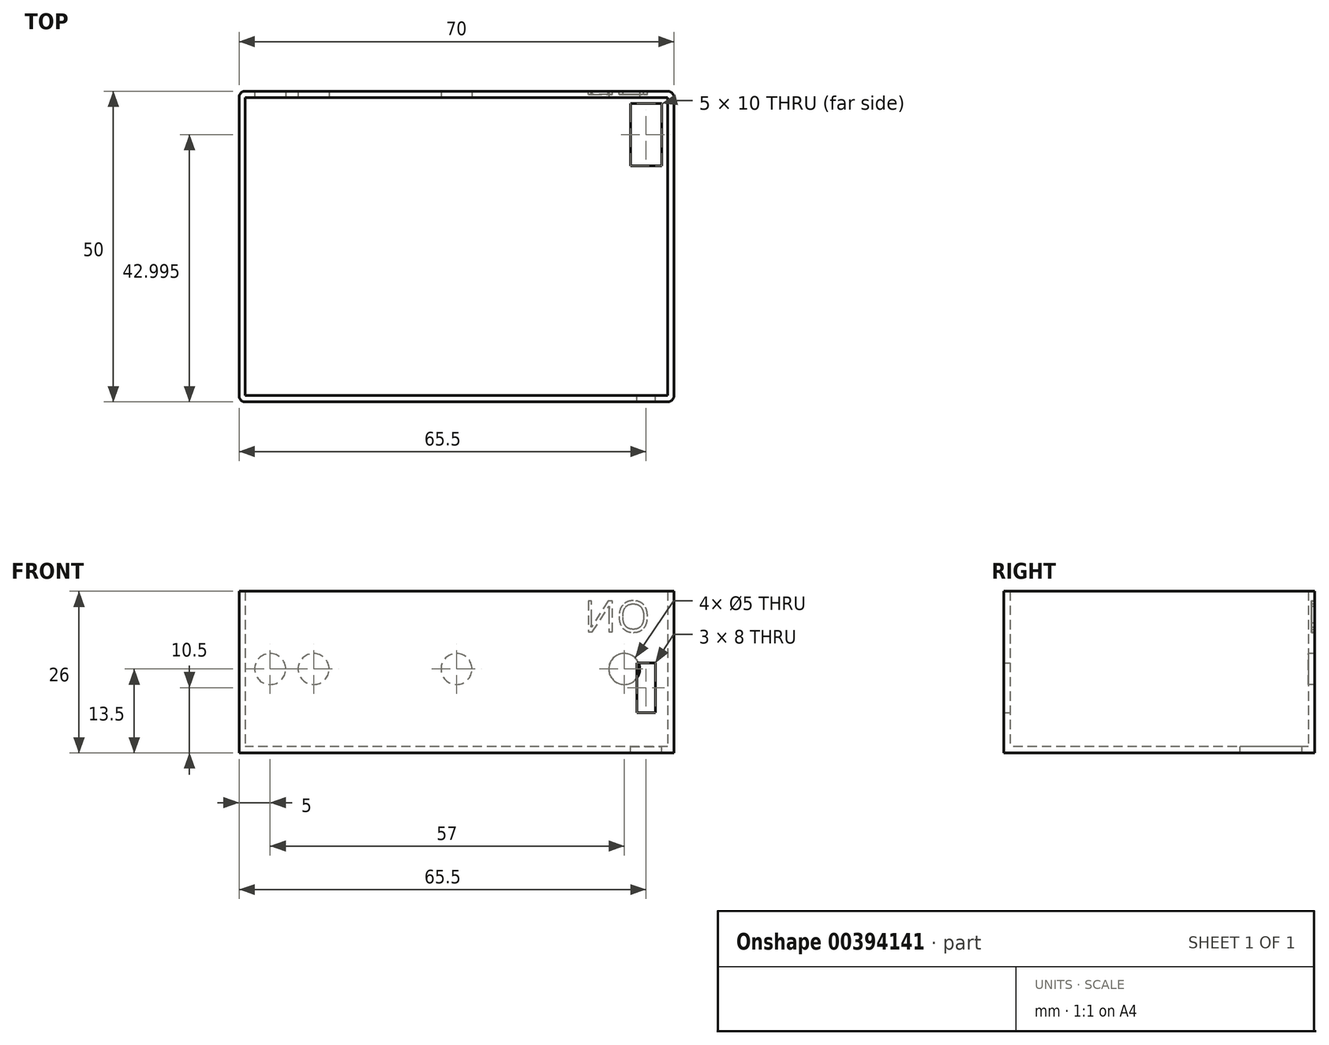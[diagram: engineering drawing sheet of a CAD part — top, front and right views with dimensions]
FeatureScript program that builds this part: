
annotation { "Feature Type Name" : "Feature", "Feature Type Description" : "" }
export const myFeature = defineFeature(function(context is Context, id is Id, definition is map)
    precondition{}
    {
        {
            var Q0;
            Q0=qCreatedBy(makeId("Top.planeOp"),FACE);
            var sketch = newSketch(context, id + "F0", { "sketchPlane" : qUnion([Q0])});
            skLineSegment(sketch, "E0.bottom", {"start": v(35, -25.8) * mm, "end": v(-35, -25.8) * mm});
            skLineSegment(sketch, "E0.top", {"start": v(35, 24.2) * mm, "end": v(-35, 24.2) * mm});
            skLineSegment(sketch, "E0.left", {"start": v(35, -25.8) * mm, "end": v(35, 24.2) * mm});
            skLineSegment(sketch, "E0.right", {"start": v(-35, -25.8) * mm, "end": v(-35, 24.2) * mm});
            skPoint(sketch, "E0.middle", {"position": v(0, -0.8) * mm});
            skSolve(sketch);
        }
        {
            var Q0;
            Q0 = qSketchRegion(id + "F0", true);
            extrude(context, id + "F1", {"entities" : qUnion([Q0]), "depth" : 1 * mm});
        }
        {
            var Q0;
            Q0=makeQuery(id+"F1.opExtrude","CAP_FACE",FACE,{"disambiguationData":[OSD([sQuery(id+"F0.wireOp",EDGE,"E0.bottom"),sQuery(id+"F0.wireOp",EDGE,"E0.top"),sQuery(id+"F0.wireOp",EDGE,"E0.left"),sQuery(id+"F0.wireOp",EDGE,"E0.right")])],"isStart":false});
            var sketch = newSketch(context, id + "F2", { "sketchPlane" : qUnion([Q0])});
            skLineSegment(sketch, "E1.0.0", {"start": v(35, -25.8) * mm, "end": v(35, 24.2) * mm});
            skLineSegment(sketch, "E1.0.1", {"start": v(35, 24.2) * mm, "end": v(-35, 24.2) * mm});
            skLineSegment(sketch, "E1.0.2", {"start": v(-35, 24.2) * mm, "end": v(-35, -25.8) * mm});
            skLineSegment(sketch, "E1.0.3", {"start": v(-35, -25.8) * mm, "end": v(35, -25.8) * mm});
            skLineSegment(sketch, "E2.0", {"start": v(-34, 23.2) * mm, "end": v(-34, -24.8) * mm});
            skLineSegment(sketch, "E2.1", {"start": v(34, 23.2) * mm, "end": v(-34, 23.2) * mm});
            skLineSegment(sketch, "E2.2", {"start": v(34, -24.8) * mm, "end": v(34, 23.2) * mm});
            skLineSegment(sketch, "E2.3", {"start": v(-34, -24.8) * mm, "end": v(34, -24.8) * mm});
            skSolve(sketch);
        }
        {
            var Q0;
            Q0=makeQuery(id+"F2.imprint","IMPRINT",FACE,{"disambiguationData":[TD([[makeQuery(id+"F2.imprint","IMPRINT",EDGE,{"derivedFrom":sQuery(id+"F2.wireOp",EDGE,"E1.0.0")}),1.0]])]});
            extrude(context, id + "F3", {"entities" : qUnion([Q0]), "operationType" : NewBodyOperationType.ADD, "depth" : 25 * mm});
        }
        {
            var Q0;
            Q0=makeQuery(id+"F3.boolean.opBoolean","MERGE",EDGE,{"derivedFrom":[makeQuery(id+"F1.opExtrude","SWEPT_EDGE",EDGE,{"disambiguationData":[OSD([sQuery(id+"F0.wireOp",EDGE,"E0.top"),sQuery(id+"F0.wireOp",EDGE,"E0.right")])]}),makeQuery(id+"F3.opExtrude","SWEPT_EDGE",EDGE,{"disambiguationData":[OSD([sQuery(id+"F2.wireOp",EDGE,"E1.0.1"),sQuery(id+"F2.wireOp",EDGE,"E1.0.2")])]})]});
            var Q1;
            Q1=makeQuery(id+"F3.boolean.opBoolean","MERGE",EDGE,{"derivedFrom":[makeQuery(id+"F1.opExtrude","SWEPT_EDGE",EDGE,{"disambiguationData":[OSD([sQuery(id+"F0.wireOp",EDGE,"E0.bottom"),sQuery(id+"F0.wireOp",EDGE,"E0.right")])]}),makeQuery(id+"F3.opExtrude","SWEPT_EDGE",EDGE,{"disambiguationData":[OSD([sQuery(id+"F2.wireOp",EDGE,"E1.0.2"),sQuery(id+"F2.wireOp",EDGE,"E1.0.3")])]})]});
            var Q2;
            Q2=makeQuery(id+"F3.boolean.opBoolean","MERGE",EDGE,{"derivedFrom":[makeQuery(id+"F1.opExtrude","SWEPT_EDGE",EDGE,{"disambiguationData":[OSD([sQuery(id+"F0.wireOp",EDGE,"E0.top"),sQuery(id+"F0.wireOp",EDGE,"E0.left")])]}),makeQuery(id+"F3.opExtrude","SWEPT_EDGE",EDGE,{"disambiguationData":[OSD([sQuery(id+"F2.wireOp",EDGE,"E1.0.0"),sQuery(id+"F2.wireOp",EDGE,"E1.0.1")])]})]});
            var Q3;
            Q3=makeQuery(id+"F3.boolean.opBoolean","MERGE",EDGE,{"derivedFrom":[makeQuery(id+"F1.opExtrude","SWEPT_EDGE",EDGE,{"disambiguationData":[OSD([sQuery(id+"F0.wireOp",EDGE,"E0.bottom"),sQuery(id+"F0.wireOp",EDGE,"E0.left")])]}),makeQuery(id+"F3.opExtrude","SWEPT_EDGE",EDGE,{"disambiguationData":[OSD([sQuery(id+"F2.wireOp",EDGE,"E1.0.0"),sQuery(id+"F2.wireOp",EDGE,"E1.0.3")])]})]});
            fillet(context, id + "F4", {"entities" : qUnion([Q0, Q1, Q2, Q3]), "radius" : 1 * mm, "tangentPropagation" : true, "allowEdgeOverflow" : false});
        }
        {
            var Q0;
            Q0=makeQuery(id+"F3.opExtrude","SWEPT_FACE",FACE,{"disambiguationData":[OSD([sQuery(id+"F2.wireOp",EDGE,"E2.3")])]});
            var sketch = newSketch(context, id + "F5", { "sketchPlane" : qUnion([Q0])});
            skLineSegment(sketch, "E3.bottom", {"start": v(-32, 14.5) * mm, "end": v(-29, 14.5) * mm});
            skLineSegment(sketch, "E3.top", {"start": v(-32, 6.5) * mm, "end": v(-29, 6.5) * mm});
            skLineSegment(sketch, "E3.left", {"start": v(-32, 14.5) * mm, "end": v(-32, 6.5) * mm});
            skLineSegment(sketch, "E3.right", {"start": v(-29, 14.5) * mm, "end": v(-29, 6.5) * mm});
            skLineSegment(sketch, "E4.0", {"start": v(-34, 26) * mm, "end": v(-34, 1) * mm});
            skSolve(sketch);
        }
        {
            var Q0;
            Q0=makeQuery(id+"F5.imprint","IMPRINT",FACE,{"disambiguationData":[TD([[makeQuery(id+"F5.imprint","IMPRINT",EDGE,{"derivedFrom":sQuery(id+"F5.wireOp",EDGE,"E3.bottom")}),-1.0]])]});
            extrude(context, id + "F6", {"entities" : qUnion([Q0]), "operationType" : NewBodyOperationType.REMOVE, "oppositeDirection" : true, "depth" : 25 * mm});
        }
        {
            var Q0;
            Q0=makeQuery(id+"F1.opExtrude","CAP_FACE",FACE,{"disambiguationData":[OSD([sQuery(id+"F0.wireOp",EDGE,"E0.bottom"),sQuery(id+"F0.wireOp",EDGE,"E0.top"),sQuery(id+"F0.wireOp",EDGE,"E0.left"),sQuery(id+"F0.wireOp",EDGE,"E0.right")])],"isStart":false});
            var sketch = newSketch(context, id + "F7", { "sketchPlane" : qUnion([Q0])});
            skLineSegment(sketch, "E5.bottom", {"start": v(28, 22.2) * mm, "end": v(33, 22.2) * mm});
            skLineSegment(sketch, "E5.top", {"start": v(28, 12.2) * mm, "end": v(33, 12.2) * mm});
            skLineSegment(sketch, "E5.left", {"start": v(28, 22.2) * mm, "end": v(28, 12.2) * mm});
            skLineSegment(sketch, "E5.right", {"start": v(33, 22.2) * mm, "end": v(33, 12.2) * mm});
            skLineSegment(sketch, "E6.0", {"start": v(34, -24.8) * mm, "end": v(34, 23.2) * mm});
            skSolve(sketch);
        }
        {
            var Q0;
            Q0=makeQuery(id+"F7.imprint","IMPRINT",FACE,{"disambiguationData":[TD([[makeQuery(id+"F7.imprint","IMPRINT",EDGE,{"derivedFrom":sQuery(id+"F7.wireOp",EDGE,"E5.bottom")}),-1.0]])]});
            extrude(context, id + "F8", {"entities" : qUnion([Q0]), "operationType" : NewBodyOperationType.REMOVE, "oppositeDirection" : true, "depth" : 25 * mm});
        }
        {
            var Q0;
            Q0=makeQuery(id+"F3.opExtrude","SWEPT_FACE",FACE,{"disambiguationData":[OSD([sQuery(id+"F2.wireOp",EDGE,"E2.1")])]});
            var sketch = newSketch(context, id + "F9", { "sketchPlane" : qUnion([Q0])});
            skCircle(sketch, "E7", {"center": v(-30, 13.5) * mm, "radius": 2.5 * mm});
            skCircle(sketch, "E8.1.0.0", {"center": v(-23, 13.5) * mm, "radius": 2.5 * mm});
            skLineSegment(sketch, "E8.direction1", {"start": v(-30, 13.5) * mm, "end": v(-23, 13.5) * mm, "construction": true});
            skSolve(sketch);
        }
        {
            var Q0;
            Q0=makeQuery(id+"F9.imprint","IMPRINT",FACE,{"disambiguationData":[TD([[makeQuery(id+"F9.imprint","IMPRINT",EDGE,{"derivedFrom":sQuery(id+"F9.wireOp",EDGE,"E7")}),1.0]])]});
            var Q1;
            Q1=makeQuery(id+"F9.imprint","IMPRINT",FACE,{"disambiguationData":[TD([[makeQuery(id+"F9.imprint","IMPRINT",EDGE,{"derivedFrom":sQuery(id+"F9.wireOp",EDGE,"E8.1.0.0")}),1.0]])]});
            extrude(context, id + "F10", {"entities" : qUnion([Q0, Q1]), "operationType" : NewBodyOperationType.REMOVE, "oppositeDirection" : true, "depth" : 25 * mm});
        }
        {
            var Q0;
            Q0=makeQuery(id+"F3.opExtrude","SWEPT_FACE",FACE,{"disambiguationData":[OSD([sQuery(id+"F2.wireOp",EDGE,"E2.1")])]});
            var sketch = newSketch(context, id + "F11", { "sketchPlane" : qUnion([Q0])});
            skCircle(sketch, "E9", {"center": v(27, 13.5) * mm, "radius": 2.5 * mm});
            skSolve(sketch);
        }
        {
            var Q0;
            Q0 = qSketchRegion(id + "F11", true);
            extrude(context, id + "F12", {"entities" : qUnion([Q0]), "operationType" : NewBodyOperationType.REMOVE, "oppositeDirection" : true, "depth" : 25 * mm});
        }
        {
            var Q0;
            Q0=makeQuery(id+"F3.opExtrude","SWEPT_FACE",FACE,{"disambiguationData":[OSD([sQuery(id+"F2.wireOp",EDGE,"E2.1")])]});
            var sketch = newSketch(context, id + "F13", { "sketchPlane" : qUnion([Q0])});
            skCircle(sketch, "E10", {"center": v(0, 13.5) * mm, "radius": 2.5 * mm});
            skSolve(sketch);
        }
        {
            var Q0;
            Q0=makeQuery(id+"F13.imprint","IMPRINT",FACE,{"disambiguationData":[TD([[makeQuery(id+"F13.imprint","IMPRINT",EDGE,{"derivedFrom":sQuery(id+"F13.wireOp",EDGE,"E10")}),1.0]])]});
            extrude(context, id + "F14", {"entities" : qUnion([Q0]), "operationType" : NewBodyOperationType.REMOVE, "oppositeDirection" : true, "depth" : 25 * mm});
        }
        {
            var Q0;
            Q0=makeQuery(id+"F45oLtiBOlkZYYh_1.boolean.opBoolean","MERGE",FACE,{"derivedFrom":[makeQuery(id+"F3.boolean.opBoolean","MERGE",FACE,{"derivedFrom":[makeQuery(id+"F1.opExtrude","SWEPT_FACE",FACE,{"disambiguationData":[OSD([sQuery(id+"F0.wireOp",EDGE,"E0.top")])]}),makeQuery(id+"F3.opExtrude","SWEPT_FACE",FACE,{"disambiguationData":[OSD([sQuery(id+"F2.wireOp",EDGE,"E1.0.1")])]})]}),makeQuery(id+"F45oLtiBOlkZYYh_1.opExtrude","SWEPT_FACE",FACE,{"disambiguationData":[OSD([sQuery(id+"FT4a1QyzRbqGLRv_1.wireOp",EDGE,"a5092cee-fa97-43a6-bd68-b99e376e83d9.0.0")])]})]});
            var sketch = newSketch(context, id + "F15", { "sketchPlane" : qUnion([Q0])});
            skText(sketch, "E11", { "text": "ON", "fontName": "OpenSans-Regular.ttf"});
            const initialGuessF15  = {"E11": [-0.03115, 0.01946, 1, 0, 0.005]};
            skSetInitialGuess(sketch, initialGuessF15);
            skSolve(sketch);
        }
        {
            var Q0;
            Q0 = qSketchRegion(id + "F15", true);
            extrude(context, id + "F16", {"entities" : qUnion([Q0]), "operationType" : NewBodyOperationType.REMOVE, "oppositeDirection" : true, "depth" : 0.5 * mm});
        }
    });
